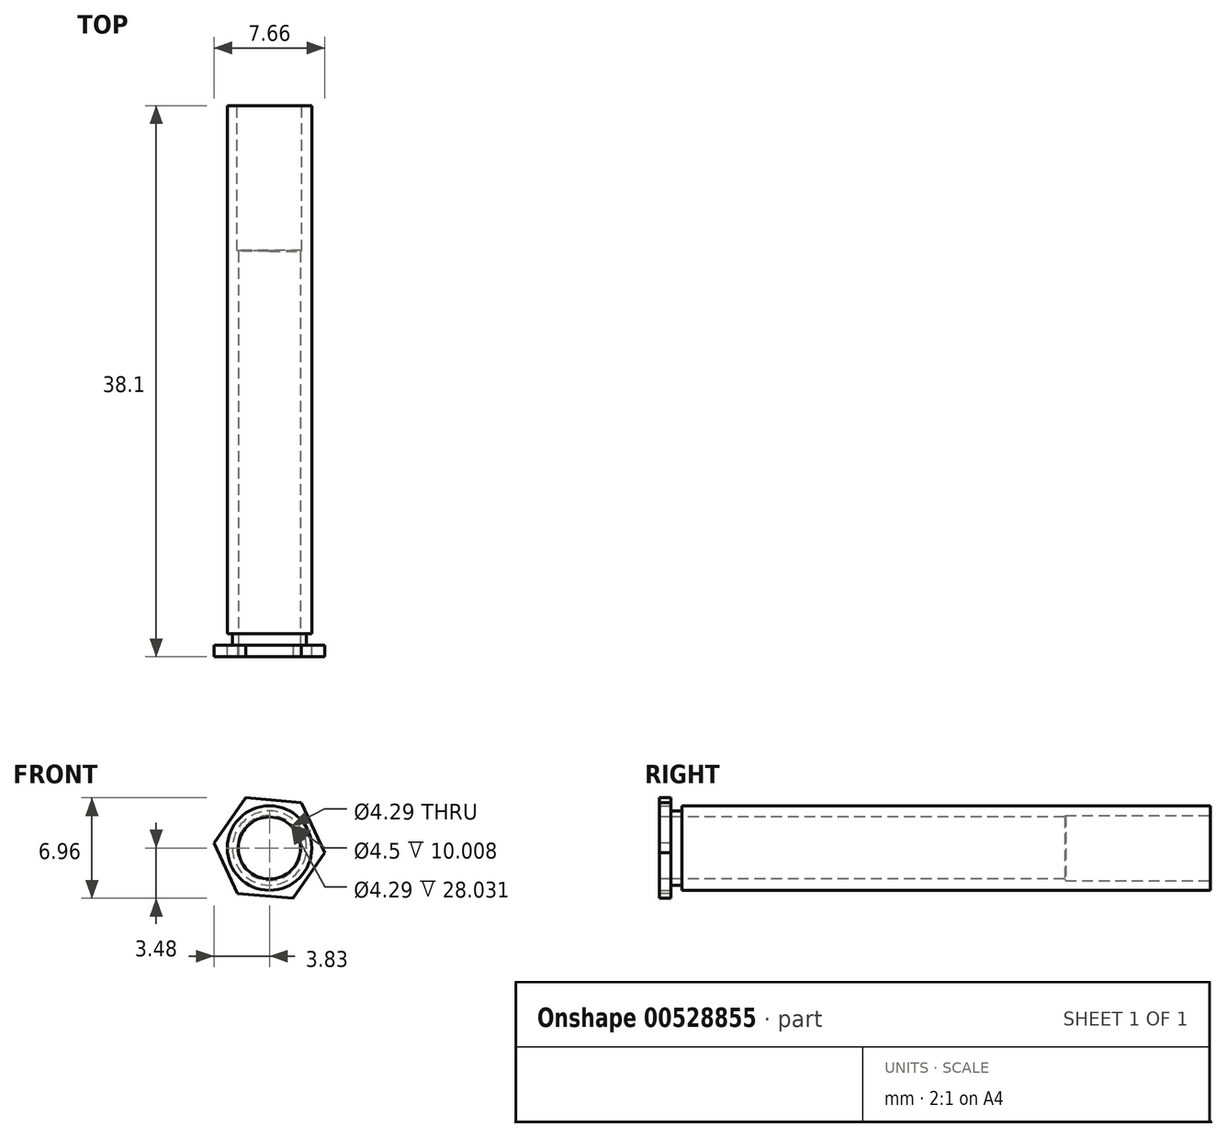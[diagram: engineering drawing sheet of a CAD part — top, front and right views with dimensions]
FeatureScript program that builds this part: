
annotation { "Feature Type Name" : "Feature", "Feature Type Description" : "" }
export const myFeature = defineFeature(function(context is Context, id is Id, definition is map)
    precondition{}
    {
        {
            var Q0;
            Q0=qCreatedBy(makeId("Front.planeOp"),FACE);
            var sketch = newSketch(context, id + "F0", { "sketchPlane" : qUnion([Q0])});
            skCircle(sketch, "E0", {"center": v(0, 0) * mm, "radius": 2.92 * mm});
            skSolve(sketch);
        }
        {
            var Q0;
            Q0 = qSketchRegion(id + "F0", true);
            extrude(context, id + "F1", {"entities" : qUnion([Q0]), "depth" : 38.1 * mm, "offsetDistance" : 25.4 * mm});
        }
        {
            var Q0;
            Q0=makeQuery(id+"F1.opExtrude","CAP_FACE",FACE,{"disambiguationData":[OSD([sQuery(id+"F0.wireOp",EDGE,"E0")])],"isStart":false});
            var sketch = newSketch(context, id + "F2", { "sketchPlane" : qUnion([Q0])});
            skCircle(sketch, "E1", {"center": v(0, 0) * mm, "radius": 3.33 * mm});
            skCircle(sketch, "E2.cCircle", {"center": v(0, 0) * mm, "radius": 3.33 * mm, "construction": true});
            skLineSegment(sketch, "E2.0", {"start": v(3.83, -0.33) * mm, "end": v(1.63, -3.48) * mm});
            skLineSegment(sketch, "E2.1", {"start": v(1.63, -3.48) * mm, "end": v(-2.2, -3.15) * mm});
            skLineSegment(sketch, "E2.2", {"start": v(-2.2, -3.15) * mm, "end": v(-3.83, 0.33) * mm});
            skLineSegment(sketch, "E2.3", {"start": v(-3.83, 0.33) * mm, "end": v(-1.63, 3.48) * mm});
            skLineSegment(sketch, "E2.4", {"start": v(-1.63, 3.48) * mm, "end": v(2.2, 3.15) * mm});
            skLineSegment(sketch, "E2.5", {"start": v(2.2, 3.15) * mm, "end": v(3.83, -0.33) * mm});
            skPoint(sketch, "E2.0.midPoint", {"position": v(2.73, -1.9) * mm});
            skSolve(sketch);
        }
        {
            var Q0;
            Q0 = qSketchRegion(id + "F2", true);
            extrude(context, id + "F3", {"entities" : qUnion([Q0]), "oppositeDirection" : true, "depth" : 0.79 * mm, "offsetDistance" : 25.4 * mm});
        }
        {
            var Q0;
            Q0=makeQuery(id+"F3.opExtrude","CAP_FACE",FACE,{"disambiguationData":[OSD([sQuery(id+"F2.wireOp",EDGE,"E2.0"),sQuery(id+"F2.wireOp",EDGE,"E2.1"),sQuery(id+"F2.wireOp",EDGE,"E2.2"),sQuery(id+"F2.wireOp",EDGE,"E2.3"),sQuery(id+"F2.wireOp",EDGE,"E2.4"),sQuery(id+"F2.wireOp",EDGE,"E2.5")])],"isStart":true});
            var sketch = newSketch(context, id + "F4", { "sketchPlane" : qUnion([Q0])});
            skSolve(sketch);
        }
        {
            var Q0;
            Q0=qCreatedBy(makeId("Right.planeOp"),FACE);
            var sketch = newSketch(context, id + "F5", { "sketchPlane" : qUnion([Q0])});
            skLineSegment(sketch, "E3.bottom", {"start": v(-36.53, 2.92) * mm, "end": v(-37.31, 2.92) * mm});
            skLineSegment(sketch, "E3.top", {"start": v(-36.53, 2.57) * mm, "end": v(-37.31, 2.57) * mm});
            skLineSegment(sketch, "E3.left", {"start": v(-36.53, 2.92) * mm, "end": v(-36.53, 2.57) * mm});
            skLineSegment(sketch, "E3.right", {"start": v(-37.31, 2.92) * mm, "end": v(-37.31, 2.57) * mm});
            skLineSegment(sketch, "E4", {"start": v(-36.56, 0) * mm, "end": v(-31.67, 0) * mm, "construction": true});
            skSolve(sketch);
        }
        {
            var Q0;
            Q0 = qSketchRegion(id + "F5", true);
            var Q1;
            Q1=sQuery(id+"F5.wireOp",EDGE,"E4");
            revolve(context, id + "F6", {"operationType" : NewBodyOperationType.REMOVE, "entities" : qUnion([Q0]), "axis" : qUnion([Q1]), "revolveType" : RevolveType.FULL, "oppositeDirection" : true});
        }
        {
            var Q0;
            Q0=makeQuery(id+"F1.opExtrude","CAP_FACE",FACE,{"disambiguationData":[OSD([sQuery(id+"F0.wireOp",EDGE,"E0")])],"isStart":true});
            var sketch = newSketch(context, id + "F7", { "sketchPlane" : qUnion([Q0])});
            skPoint(sketch, "E5", {"position": v(0, 0) * mm});
            skSolve(sketch);
        }
        {
            var Q0;
            Q0=sQuery(id+"F7.wireOp",VERTEX,"E5");
            var Q1;
            Q1=makeQuery(id+"F1.opExtrude","SWEPT_BODY",BODY,{"disambiguationData":[OSD([sQuery(id+"F0.wireOp",EDGE,"E0")])]});
            var Q2;
            Q2=makeQuery(id+"F3.opExtrude","SWEPT_BODY",BODY,{"disambiguationData":[OSD([sQuery(id+"F2.wireOp",EDGE,"E2.0"),sQuery(id+"F2.wireOp",EDGE,"E2.1"),sQuery(id+"F2.wireOp",EDGE,"E2.2"),sQuery(id+"F2.wireOp",EDGE,"E2.3"),sQuery(id+"F2.wireOp",EDGE,"E2.4"),sQuery(id+"F2.wireOp",EDGE,"E2.5")])]});
            hole(context, id + "F8", {"style" : HoleStyle.SIMPLE, "endStyle" : HoleEndStyle.BLIND, "standardTappedOrClearance" : lookupTablePath({ "standard" : "ANSI", "fit" : "Normal (ASME)", "size" : "#8", "type" : "Clearance" }), "standardBlindInLast" : lookupTablePath({ "fit" : "Free", "standard" : "ANSI", "size" : "#8", "type" : "Clearance" }), "holeDiameter" : 4.5 * mm, "holeDepth" : 10 * mm, "tappedDepth" : 5.08 * mm, "tapClearance" : 3, "locations" : qUnion([Q0]), "scope" : qUnion([Q1, Q2]), "majorDiameter" : 6.35 * mm});
        }
        {
            var Q0;
            Q0=makeQuery(id+"F4.imprint","IMPRINT",FACE,{"disambiguationData":[TD([[makeQuery(id+"F4.imprint","IMPRINT",EDGE,{"derivedFrom":makeQuery(id+"F3.opExtrude","CAP_EDGE",EDGE,{"disambiguationData":[OSD([sQuery(id+"F2.wireOp",EDGE,"E2.0")])],"isStart":true})}),-1.0]])]});
            var sketch = newSketch(context, id + "F9", { "sketchPlane" : qUnion([Q0])});
            skCircle(sketch, "E6", {"center": v(0, 0) * mm, "radius": 2.15 * mm});
            skSolve(sketch);
        }
        {
            var Q0;
            Q0 = qSketchRegion(id + "F9", true);
            extrude(context, id + "F10", {"entities" : qUnion([Q0]), "operationType" : NewBodyOperationType.REMOVE, "oppositeDirection" : true, "depth" : 35.56 * mm, "offsetDistance" : 25.4 * mm});
        }
    });
